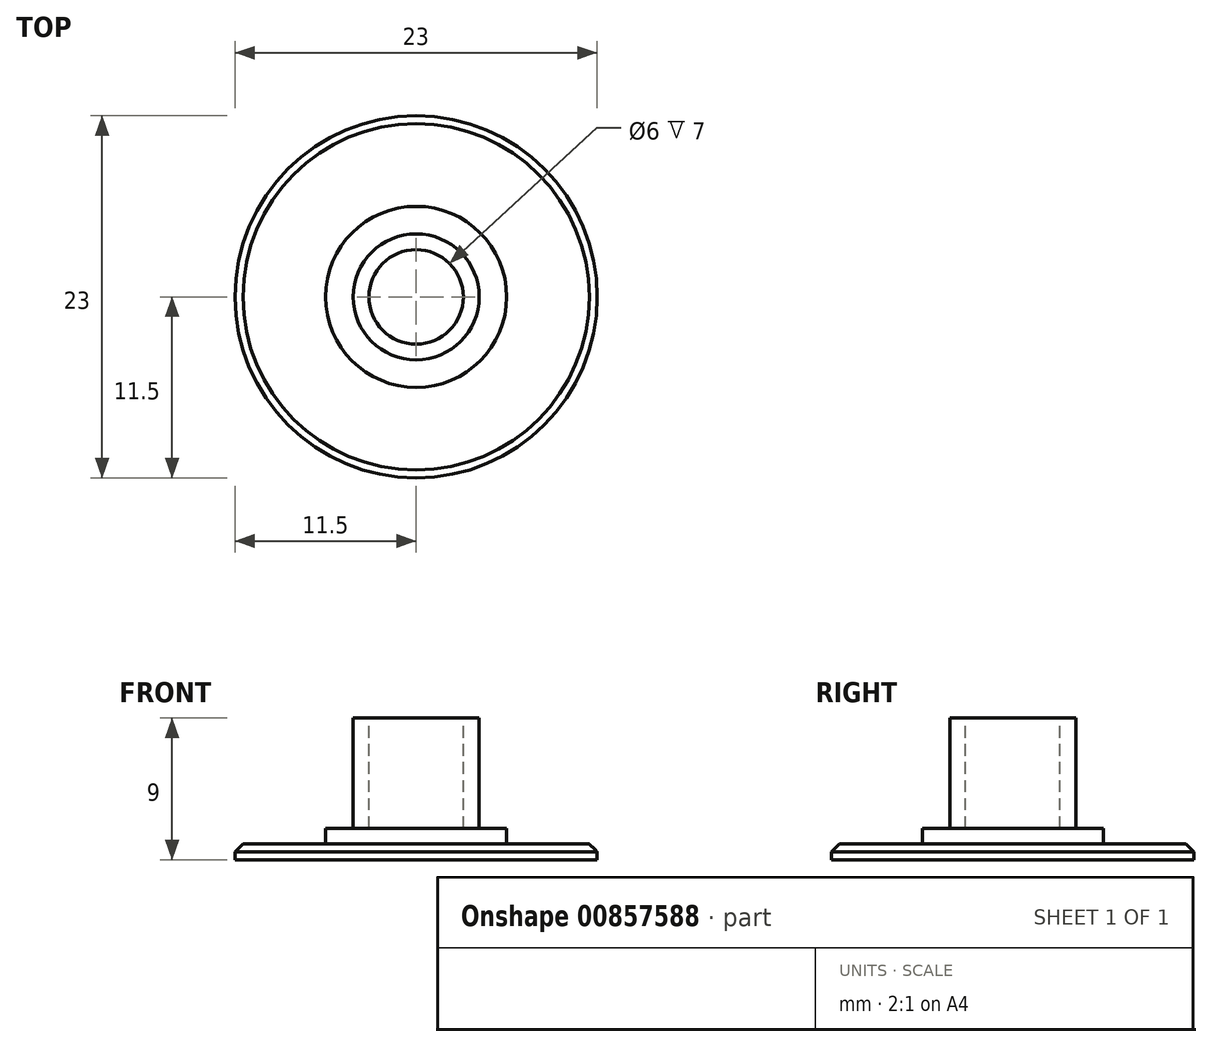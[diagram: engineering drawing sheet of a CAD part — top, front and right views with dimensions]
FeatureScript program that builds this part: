
annotation { "Feature Type Name" : "Feature", "Feature Type Description" : "" }
export const myFeature = defineFeature(function(context is Context, id is Id, definition is map)
    precondition{}
    {
        {
            var Q0;
            Q0=qCreatedBy(makeId("Top.planeOp"),FACE);
            var sketch = newSketch(context, id + "F0", { "sketchPlane" : qUnion([Q0])});
            skCircle(sketch, "E0", {"center": v(0, 0) * mm, "radius": 11.5 * mm});
            skSolve(sketch);
        }
        {
            var Q0;
            Q0=qSketchRegion(id+"F0",true);
            extrude(context, id + "F1", {"entities" : qUnion([Q0]), "depth" : 1 * mm, "offsetDistance" : 25 * mm});
        }
        {
            var Q0;
            Q0=makeQuery(id+"F1.opExtrude","CAP_FACE",FACE,{"disambiguationData":[OSD([sQuery(id+"F0.wireOp",EDGE,"E0")])],"isStart":false});
            var sketch = newSketch(context, id + "F2", { "sketchPlane" : qUnion([Q0])});
            skCircle(sketch, "E1", {"center": v(0, 0) * mm, "radius": 5.75 * mm});
            skSolve(sketch);
        }
        {
            var Q0;
            Q0=qSketchRegion(id+"F2",true);
            extrude(context, id + "F3", {"entities" : qUnion([Q0]), "operationType" : NewBodyOperationType.ADD, "depth" : 1 * mm, "offsetDistance" : 25 * mm});
        }
        {
            var Q0;
            Q0=makeQuery(id+"F3.opExtrude","CAP_FACE",FACE,{"disambiguationData":[OSD([sQuery(id+"F2.wireOp",EDGE,"E1")])],"isStart":false});
            var sketch = newSketch(context, id + "F4", { "sketchPlane" : qUnion([Q0])});
            skCircle(sketch, "E2", {"center": v(0, 0) * mm, "radius": 4 * mm});
            skSolve(sketch);
        }
        {
            var Q0;
            Q0=qSketchRegion(id+"F4",true);
            extrude(context, id + "F5", {"entities" : qUnion([Q0]), "operationType" : NewBodyOperationType.ADD, "depth" : 7 * mm, "offsetDistance" : 25 * mm});
        }
        {
            var Q0;
            Q0=makeQuery(id+"F5.opExtrude","CAP_FACE",FACE,{"disambiguationData":[OSD([sQuery(id+"F4.wireOp",EDGE,"E2")])],"isStart":false});
            var sketch = newSketch(context, id + "F6", { "sketchPlane" : qUnion([Q0])});
            skCircle(sketch, "E3", {"center": v(0, 0) * mm, "radius": 3 * mm});
            skSolve(sketch);
        }
        {
            var Q0;
            Q0=qSketchRegion(id+"F6",true);
            extrude(context, id + "F7", {"entities" : qUnion([Q0]), "operationType" : NewBodyOperationType.REMOVE, "oppositeDirection" : true, "depth" : 7 * mm, "offsetDistance" : 25 * mm});
        }
        {
            var Q0;
            Q0=makeQuery(id+"F1.opExtrude","CAP_EDGE",EDGE,{"disambiguationData":[OSD([sQuery(id+"F0.wireOp",EDGE,"E0")])],"isStart":false});
            chamfer(context, id + "F8", {"entities" : qUnion([Q0]), "width" : .5 * mm, "tangentPropagation" : true});
        }
    });
